# Revit family: Grohe_Thermostat_Smartcontrol_29508KF0
name_source: partatom
category: Plumbing Fixtures
units: mm (PartAtom-declared; Revit-internal decimal feet)

## family parameters
Cut with Voids When Loaded = No
Host = Face
OmniClass Number = 23.45.05.00
OmniClass Title = Sanitary Equipment
Part Type = Normal
Room Calculation Point = No
Round Connector Dimension = Use Diameter
Shared = No

## types (1)
- SMARTCONTROL Thermostat (29508KF0)
    Assembly Code = D2010
    AssetType = Fixed
    BIMObjectName = Grohe_Thermostat_Smartcontrol_29508KF0
    CO2NeutralProduction = GROHE is one of the first leading manufacturer within the sanitary industry having a CO2-neutral production.
    CW Connection = No
    ClassificationName = Uniclass2015
    ClassificationValue = Pr_65_54_95_88
    Color = Matt Black
    Cost = 0 $
    Default Elevation = 0 mm  [stored 0 ft]
    Description = SMARTCONTROL Thermostat (29508KF0)
    DimensionsDocumentLink = https://cdn.cloud.grohe.com
    DocumentationCertificates = https://www.bimstore.co
    DocumentationInstallationGuide = https://www.bimstore.co
    DocumentationLiterature = https://www.bimstore.co
    DocumentationMaintenance = https://www.bimstore.co
    DocumentationTechnical = https://www.bimstore.co
    DurationUnit = Years
    EF000010 = Finishing section
    EF001707 = 70 °C
    EF002149 = TRUE
    EF002286 = not applicable
    EF002671 = Black
    EF005464 = 0
    EF011775 = not applicable
    EF011779 = TRUE
    EF012753 = 36.00
    EF014578 = not applicable
    EF014591 = FALSE
    EF016731 = Group I,<= 20 dB(A)
    EF020105 = Yes
    EF020774 = TRUE
    EF020775 = FALSE
    EF020776 = FALSE
    EF020777 = FALSE
    EF020778 = FALSE
    EF020779 = FALSE
    EF020780 = not relevant
    EF020781 = Other
    EF020782 = Brass
    EF020783 = Other
    EF020784 = Other
    EF020785 = not applicable
    EF020786 = 3
    EF020787 = Group II, <=30 dB(A)
    EF020788 = FALSE
    EF020789 = 0 mm  [stored 0 ft]
    EF020790 = TRUE
    EF020963 = TRUE
    EF021855 = FALSE
    EF022042 = D
    EF023686 = Other
    EF023687 = FALSE
    EF023957 = TRUE
    EFDE0022 = None
    EFSE0002 = TRUE
    Ecojoy = No
    ExpectedLife = 0
    FullRecyclabilityOfPlastic = All plastic components are fully recyclable
    GROHESocialCommittment = green.grohe.com/social_engagement
    GROHESustainability = green.grohe.com
    HW Connection = No
    IfcExportAs = IfcPipeFitting
    IfcExportType = IfcPipeFittingType
    Keynote = N13
    Manufacturer = Grohe
    ManufacturerName = Grohe
    Model = SMARTCONTROL Thermostat (29508KF0)
    ModelNumber = 29508KF0
    ModelReference = SMARTCONTROL Thermostat (29508KF0)
    NBSDescription = Thermostatic mixing valves
    NBSObjectName = Grohe - Thermostatic mixing valves
    NBSReference = 90-10-90/370
    NominalDepth = 0 mm  [stored 0 ft]
    NominalHeight = 0 mm  [stored 0 ft]
    NominalLength = 0 mm  [stored 0 ft]
    PQDiagramLink = https://cdn.cloud.grohe.com
    PrimaryMaterial = Grohe_MattBlack
    ProductDescription = set for final installation for GROHE Rapido SmartBox (35 600/35 604)

metal wall escutcheon with GROHE FastFixation 

(covered escutcheon and shaft sealing, covered 

fixing), retroactively 6° adjustable

GROHE Long-Life Shine finish

GROHE SmartControl push for ON-OFF, turn for volume adjustment from GROHE Water Saving to Full Flow, exchangeable symbols

GROHE TurboStat compact cartridge with wax thermoelement

GROHE ProGrip with knurl structure

GROHE SafeStop safety button at 38°C

GROHE SafeStop Plus optional temperature limiter at 43°C or 46°C included

built-in non return valves and dirt strainers

multiple outlets can be run simultaneously

without roughing-in set

flow performance: 

outlet A = 23 l/min 

outlet B = 27 l/min 

outlet C = 23 l/min

outlet A + B = 33 l/min

outlet A + B + C = 36 l/min
    ProductNumber = 29508KF0
    ProductPageURL = https://www.grohe.co.uk
    ProductShortText = Thermostat for concealed installation with 3 valves
    ProductType = Thermostat
    ProductionYear = 2023
    SustainabilityAward = green.grohe.com/awards
    SustainabilityReport = green.grohe.com/reporting
    TPIDocumentLink = https://cdn.cloud.grohe.com
    Type Comments = SMARTCONTROL Thermostat (29508KF0)
    TypeName = SMARTCONTROL Thermostat (29508KF0)
    URL = https://www.grohe.co.uk
    Vent Connection = No
    WarrantyDurationLabor = 0
    WarrantyDurationParts = 0
    WarrantyDurationUnit = Years
    Waste Connection = No
    _BSBibleVersion = 17
    _BimSpecGuid = 0
    _CurrentRevision = 1
    _DistributedBy = https://www.bimstore.co
    _ObjectUserGuide = https://www.bimstore.co

note: [stored X ft] marks values corroborated as IEEE doubles in the binary element streams (Revit-internal decimal feet)

## geometry (parser evidence)
native form markers: Sweep x2
no freeform markers — native parametric forms only
